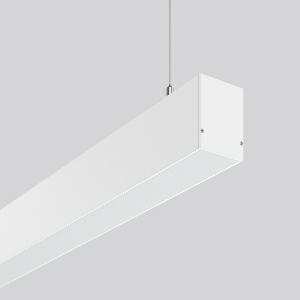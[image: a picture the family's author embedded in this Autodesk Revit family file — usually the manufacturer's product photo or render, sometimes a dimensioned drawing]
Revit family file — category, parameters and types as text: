
# Revit family: less_is_more_50_312317_002_e6c7
name_source: partatom
category: Lighting Fixtures
units: mm (PartAtom-declared; Revit-internal decimal feet)

## family parameters
Cut with Voids When Loaded = No
Host = Face
Light Source = No
Part Type = Normal
Room Calculation Point = No
Round Connector Dimension = Use Diameter
Shared = No

## types (1)
- LESS IS MORE 50 (1 x LED Modul 830, 3850 lm, 3000)
    Apparent Load = 34 VA
    CIE Flux Codes = 49 80 96 63 100
    Color Rendering = 80
    Color Temperature = 3000
    Default Elevation = 1800 mm
    Description = Series: LESS IS MORE 50
Linear pendant luminaire for aesthetically sophisticated lighting. Housing: extruded aluminium profile, powder-coated. End cap aluminium powder-coated. Canopy made of aluminium, powder-coated. Diffuser made of non-yellowing plastic (PMMA), opal. Direct 65%, indirect 35% light emission. Suitable for pendant. 2-point steel cable suspension freely positionable and infinitely height-adjustable. Special lengths available on request. LED unit with integrated converter interchangeable and removable. Suitable for through-wiring. With sensors or as a safety luminaire on request. 
Colour: traffic white, matt (RAL 9016)
Length: 847 mm
Width: 57 mm
Height: 75 mm
Suspension length: 2000 mm
Lamp: LED
Socket: without socket
Colour temperature: 3000K
Colour rendering index (CRI): 80
Light source: LED
Socket lamp2: Without base
Colour temperature: 3000K
System power: 34 W
Rated luminous flux: 3850 lm
Luminous efficiency: 113 lm/W
Control gear: Regulated power supply
Control gear: Regulated power supply
Protection class: I
Type of protection: IP 20
    Height = 75 mm
    Lamp = 1 x LED Modul 830
    Lamp Light Flux = 3850 lm
    Lamp count = 1
    Length = 847 mm
    Lifetime = 50000 h
    Luminous efficacy = 113 lm/W
    Manufacturer = RZB
    ModVariant = No
    Model = 312317.002
    Mounting Place = Ceiling
    Mounting Type = Pendant
    Number of Poles = 1
    OnlyDefault = Yes
    Power Factor = 1
    Product Name = LESS IS MORE 50
    Product group = Pendant LED linear luminaires
    ProductGroupID = 907
    Protection Class = Protection class I
    Protection Degree = IP 20
    RLX_Detail_Level = 1
    RLX_Emergency_Light_Flux = 0 lm
    RLX_Emergency_Type = 0
    RLX_Emergency_Type_DB = No
    RlxData = <blob elided: 31617 chars, md5=2a3732f7>
    Socket = socket
    Standby Power = 0 W
    System Light Flux = 3850 lm
    System Power = 34 W
    Type Comments = Product without accessories
    Type Image = 312318.002.jpg
    URL = http://relux.com
    VarID = ---
    Voltage = 230 V
    Voltage Range = 220-240 V
    Weight = 0.00 kg
    Width = 57 mm

## geometry (parser evidence)
native form markers: Blend x4, Sweep x14
no freeform markers — native parametric forms only
